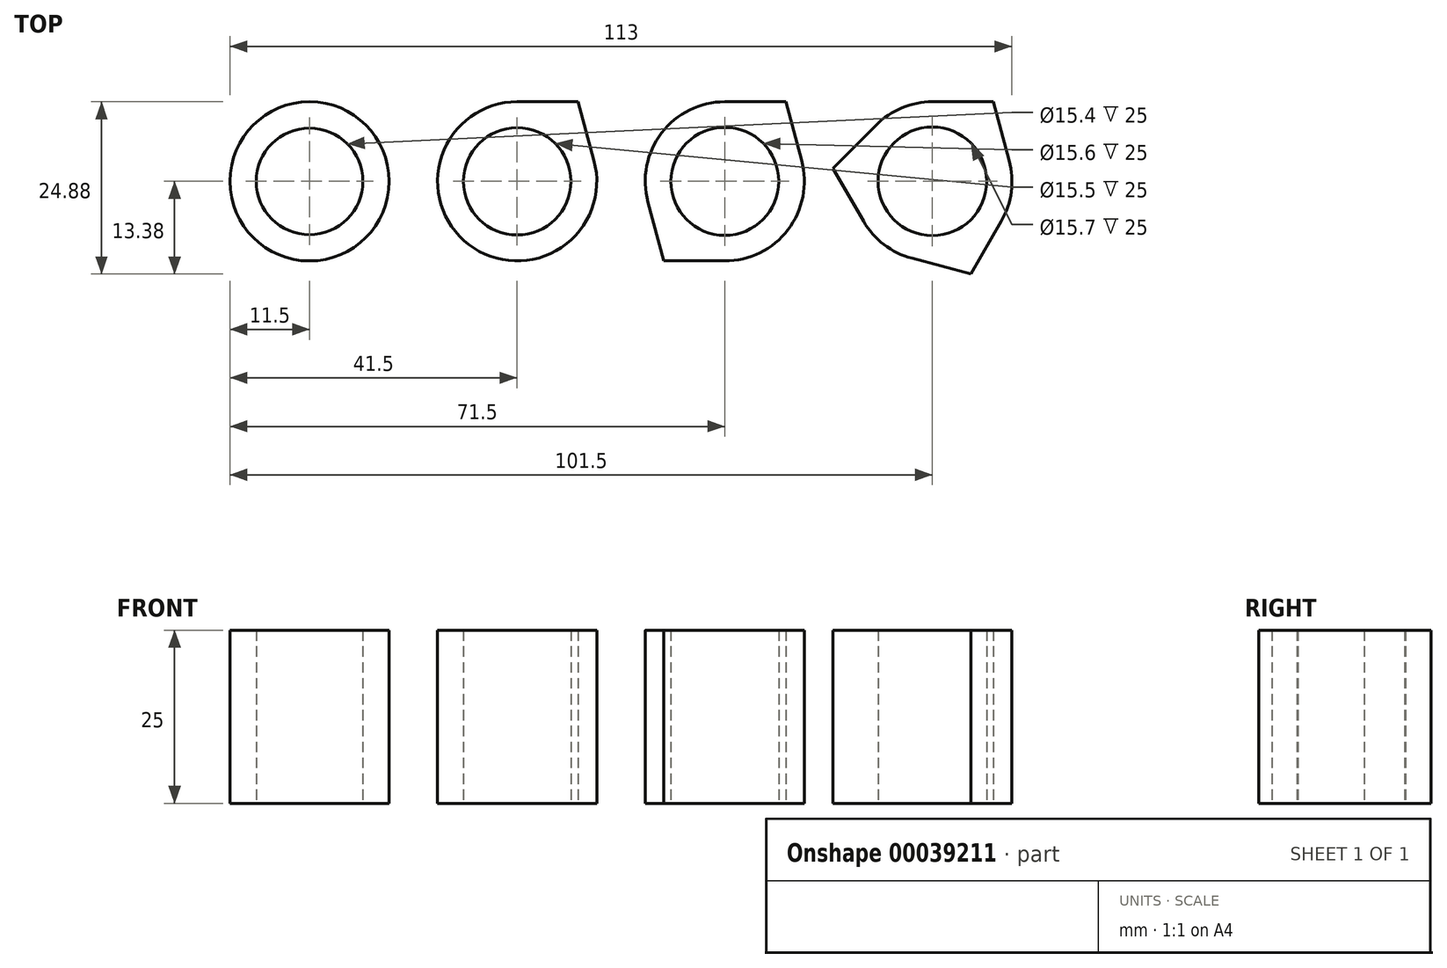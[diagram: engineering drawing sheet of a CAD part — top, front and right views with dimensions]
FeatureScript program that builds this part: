
annotation { "Feature Type Name" : "Feature", "Feature Type Description" : "" }
export const myFeature = defineFeature(function(context is Context, id is Id, definition is map)
    precondition{}
    {
        {
            var Q0;
            Q0=qCreatedBy(makeId("Top.planeOp"),FACE);
            var sketch = newSketch(context, id + "F0", { "sketchPlane" : qUnion([Q0])});
            skCircle(sketch, "E0", {"center": v(-30, 0) * mm, "radius": 11.5 * mm});
            skCircle(sketch, "E1", {"center": v(-30, 0) * mm, "radius": 7.75 * mm});
            skCircle(sketch, "E2", {"center": v(0, 0) * mm, "radius": 11.5 * mm});
            skCircle(sketch, "E3", {"center": v(0, 0) * mm, "radius": 7.8 * mm});
            skCircle(sketch, "E4", {"center": v(30, 0) * mm, "radius": 11.5 * mm});
            skCircle(sketch, "E5", {"center": v(30, 0) * mm, "radius": 7.85 * mm});
            skLineSegment(sketch, "E6", {"start": v(-30, 11.5) * mm, "end": v(-21.2, 11.5) * mm});
            skLineSegment(sketch, "E7", {"start": v(-21.2, 11.5) * mm, "end": v(-18.9, 3) * mm});
            skLineSegment(sketch, "E8", {"start": v(8.8, 11.5) * mm, "end": v(11.1, 3) * mm});
            skLineSegment(sketch, "E9", {"start": v(0, 11.5) * mm, "end": v(8.8, 11.5) * mm});
            skLineSegment(sketch, "E10.1.0", {"start": v(-8.8, -11.5) * mm, "end": v(-11.1, -3) * mm});
            skLineSegment(sketch, "E10.1.1", {"start": v(0, -11.5) * mm, "end": v(-8.8, -11.5) * mm});
            skLineSegment(sketch, "E11", {"start": v(38.8, 11.5) * mm, "end": v(41.1, 3) * mm});
            skLineSegment(sketch, "E12", {"start": v(30, 11.5) * mm, "end": v(38.8, 11.5) * mm});
            skLineSegment(sketch, "E13.1.0", {"start": v(15.64, 1.88) * mm, "end": v(21.85, 8.11) * mm});
            skLineSegment(sketch, "E13.1.1", {"start": v(20.04, -5.75) * mm, "end": v(15.64, 1.88) * mm});
            skLineSegment(sketch, "E13.2.0", {"start": v(35.56, -13.38) * mm, "end": v(27.05, -11.11) * mm});
            skLineSegment(sketch, "E13.2.1", {"start": v(39.96, -5.75) * mm, "end": v(35.56, -13.38) * mm});
            skCircle(sketch, "E14", {"center": v(-60, 0) * mm, "radius": 11.5 * mm});
            skCircle(sketch, "E15", {"center": v(-60, 0) * mm, "radius": 7.7 * mm});
            skSolve(sketch);
        }
        {
            var Q0;
            Q0 = qSketchRegion(id + "F0", true);
            extrude(context, id + "F1", {"entities" : qUnion([Q0]), "depth" : 25 * mm});
        }
    });
